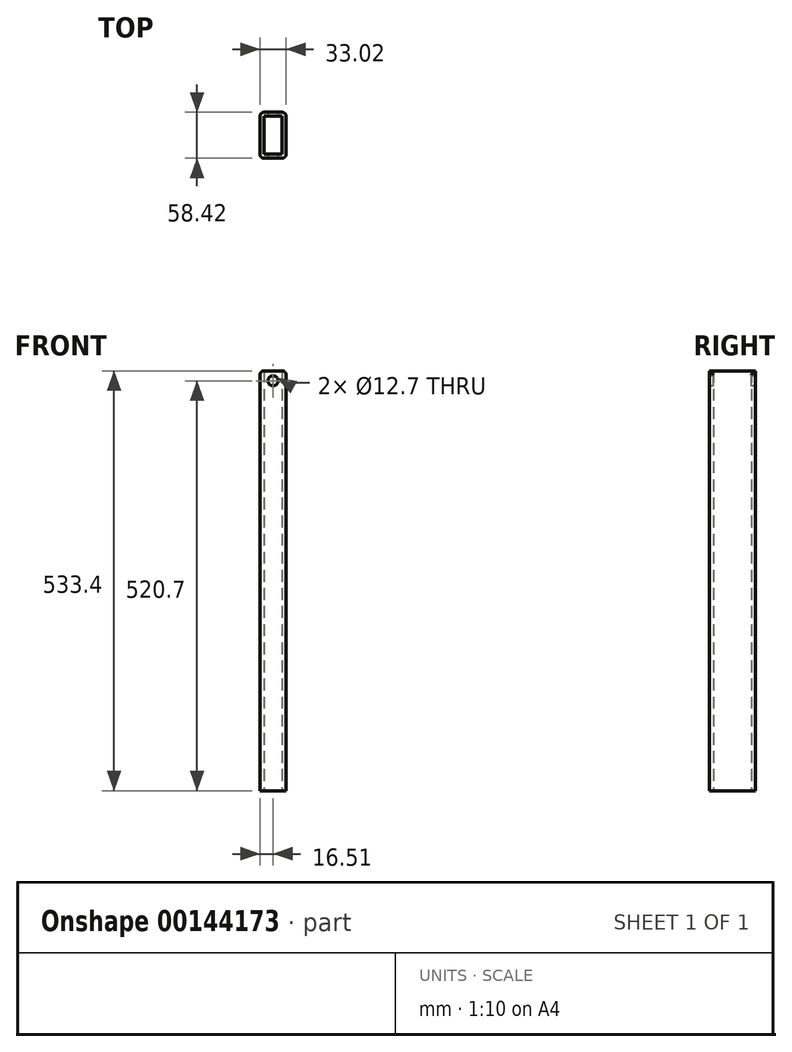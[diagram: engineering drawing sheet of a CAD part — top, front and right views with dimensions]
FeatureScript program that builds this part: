
annotation { "Feature Type Name" : "Feature", "Feature Type Description" : "" }
export const myFeature = defineFeature(function(context is Context, id is Id, definition is map)
    precondition{}
    {
        {
            var Q0;
            Q0=qCreatedBy(makeId("Front.planeOp"),FACE);
            var sketch = newSketch(context, id + "F0", { "sketchPlane" : qUnion([Q0])});
            skLineSegment(sketch, "E0.bottom", {"start": v(0, 0) * mm, "end": v(33.02, 0) * mm});
            skLineSegment(sketch, "E0.top", {"start": v(0, -533.4) * mm, "end": v(33.02, -533.4) * mm});
            skLineSegment(sketch, "E0.left", {"start": v(0, 0) * mm, "end": v(0, -533.4) * mm});
            skLineSegment(sketch, "E0.right", {"start": v(33.02, 0) * mm, "end": v(33.02, -533.4) * mm});
            skSolve(sketch);
        }
        {
            var Q0;
            Q0=makeQuery(id+"F0.imprint","IMPRINT",FACE,{"disambiguationData":[TD([[makeQuery(id+"F0.imprint","IMPRINT",EDGE,{"derivedFrom":sQuery(id+"F0.wireOp",EDGE,"E0.bottom")}),-1.0]])]});
            extrude(context, id + "F1", {"entities" : qUnion([Q0]), "depth" : 58.42 * mm});
        }
        {
            var Q0;
            Q0=makeQuery(id+"F1.opExtrude","CAP_FACE",FACE,{"disambiguationData":[OSD([sQuery(id+"F0.wireOp",EDGE,"E0.bottom"),sQuery(id+"F0.wireOp",EDGE,"E0.top"),sQuery(id+"F0.wireOp",EDGE,"E0.left"),sQuery(id+"F0.wireOp",EDGE,"E0.right")])],"isStart":false});
            var sketch = newSketch(context, id + "F2", { "sketchPlane" : qUnion([Q0])});
            skPoint(sketch, "E1", {"position": v(16.51, 0) * mm});
            skLineSegment(sketch, "E2", {"start": v(16.51, 0) * mm, "end": v(16.51, -12.7) * mm, "construction": true});
            skSolve(sketch);
        }
        {
            var Q0;
            Q0=makeQuery(id+"F1.opExtrude","SWEPT_FACE",FACE,{"disambiguationData":[OSD([sQuery(id+"F0.wireOp",EDGE,"E0.bottom")])]});
            var Q1;
            Q1=makeQuery(id+"F1.opExtrude","SWEPT_FACE",FACE,{"disambiguationData":[OSD([sQuery(id+"F0.wireOp",EDGE,"E0.top")])]});
            shell(context, id + "F3", {"entities" : qUnion([Q0, Q1]), "thickness" : 5.08 * mm});
        }
        {
            var Q0;
            Q0=sQuery(id+"F2.wireOp",VERTEX,"E2.end");
            var Q1;
            Q1=makeQuery(id+"F1.opExtrude","SWEPT_BODY",BODY,{"disambiguationData":[OSD([sQuery(id+"F0.wireOp",EDGE,"E0.bottom"),sQuery(id+"F0.wireOp",EDGE,"E0.top"),sQuery(id+"F0.wireOp",EDGE,"E0.left"),sQuery(id+"F0.wireOp",EDGE,"E0.right")])]});
            hole(context, id + "F4", {"style" : HoleStyle.SIMPLE, "endStyle" : HoleEndStyle.THROUGH, "holeDiameter" : 12.7 * mm, "locations" : qUnion([Q0]), "scope" : qUnion([Q1]), "isTappedThrough" : true});
        }
        {
            var Q0;
            Q0=makeQuery(id+"F1.opExtrude","CAP_EDGE",EDGE,{"disambiguationData":[OSD([sQuery(id+"F0.wireOp",EDGE,"E0.left")])],"isStart":false});
            var Q1;
            Q1=makeQuery(id+"F1.opExtrude","CAP_EDGE",EDGE,{"disambiguationData":[OSD([sQuery(id+"F0.wireOp",EDGE,"E0.right")])],"isStart":false});
            var Q2;
            Q2=makeQuery(id+"F1.opExtrude","CAP_EDGE",EDGE,{"disambiguationData":[OSD([sQuery(id+"F0.wireOp",EDGE,"E0.right")])],"isStart":true});
            var Q3;
            Q3=makeQuery(id+"F1.opExtrude","CAP_EDGE",EDGE,{"disambiguationData":[OSD([sQuery(id+"F0.wireOp",EDGE,"E0.left")])],"isStart":true});
            var Q4;
            Q4=makeQuery(id+"F1.opExtrude","SWEPT_EDGE",EDGE,{"disambiguationData":[OSD([sQuery(id+"F0.wireOp",EDGE,"E0.bottom"),sQuery(id+"F0.wireOp",EDGE,"E0.right")])]});
            var Q5;
            Q5=makeQuery(id+"F1.opExtrude","SWEPT_EDGE",EDGE,{"disambiguationData":[OSD([sQuery(id+"F0.wireOp",EDGE,"E0.bottom"),sQuery(id+"F0.wireOp",EDGE,"E0.left")])]});
            fillet(context, id + "F5", {"entities" : qUnion([Q0, Q1, Q2, Q3, Q4, Q5]), "radius" : 5.08 * mm, "tangentPropagation" : true, "allowEdgeOverflow" : false});
        }
    });
